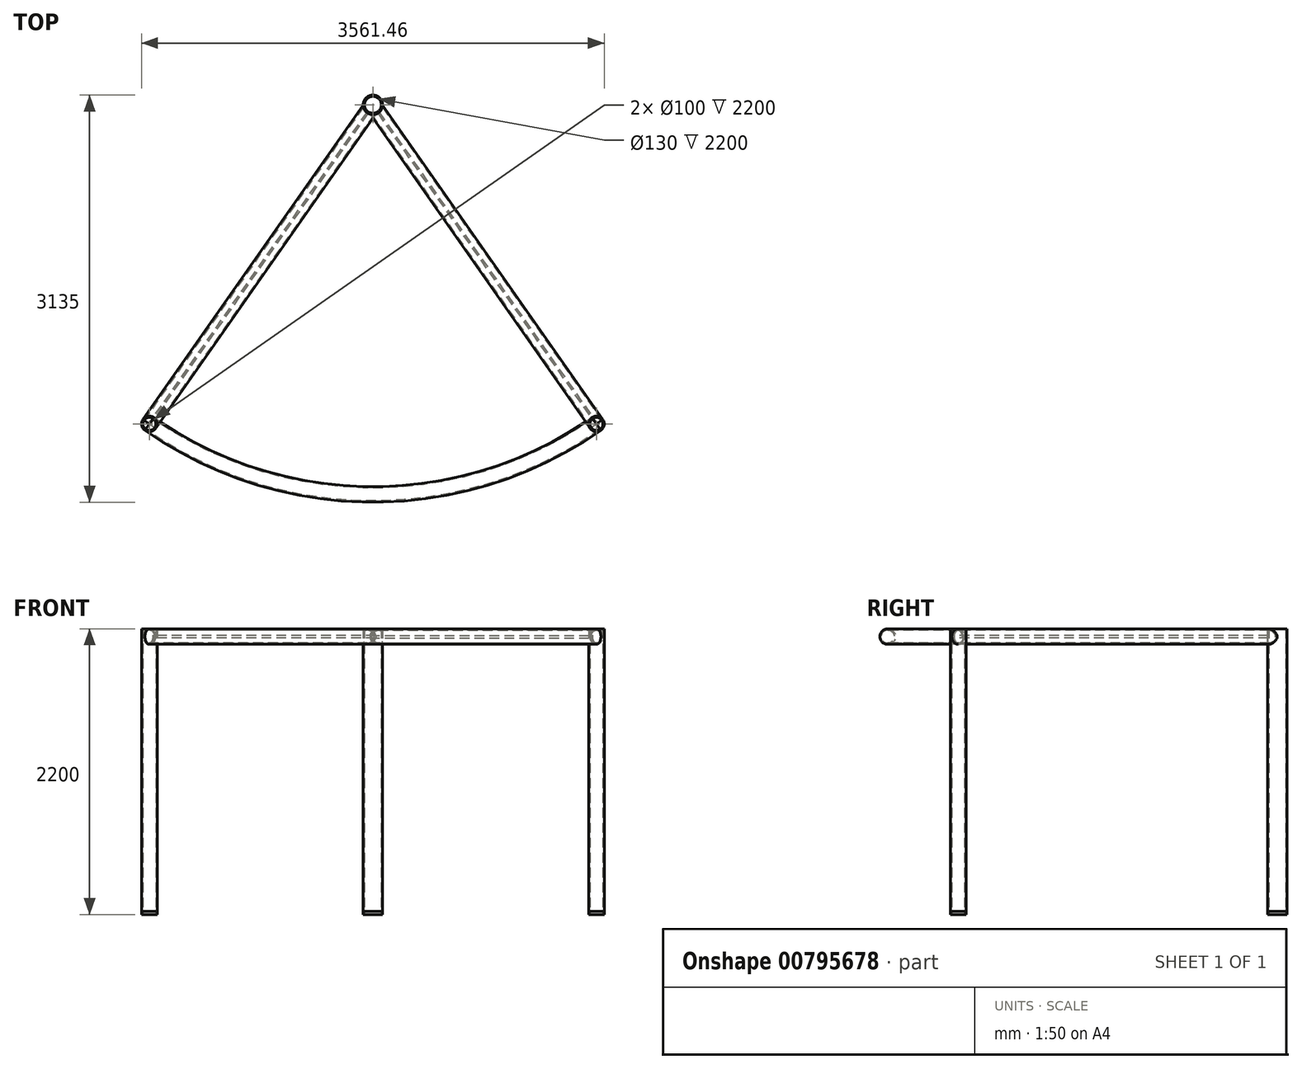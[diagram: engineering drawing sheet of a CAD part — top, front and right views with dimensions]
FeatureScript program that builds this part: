
annotation { "Feature Type Name" : "Feature", "Feature Type Description" : "" }
export const myFeature = defineFeature(function(context is Context, id is Id, definition is map)
    precondition{}
    {
        {
            var Q0;
            Q0=qCreatedBy(makeId("Front.planeOp"),FACE);
            var sketch = newSketch(context, id + "F0", { "sketchPlane" : qUnion([Q0])});
            skLineSegment(sketch, "E0.bottom", {"start": v(110, -110) * mm, "end": v(-110, -110) * mm});
            skLineSegment(sketch, "E0.top", {"start": v(110, 110) * mm, "end": v(-110, 110) * mm});
            skLineSegment(sketch, "E0.left", {"start": v(110, -110) * mm, "end": v(110, 110) * mm});
            skLineSegment(sketch, "E0.right", {"start": v(-110, -110) * mm, "end": v(-110, 110) * mm});
            skPoint(sketch, "E0.middle", {"position": v(0, 0) * mm});
            skSolve(sketch);
        }
        {
            var Q0;
            Q0 = qSketchRegion(id + "F0", true);
            extrude(context, id + "F1", {"entities" : qUnion([Q0]), "depth" : 3 * mm, "offsetDistance" : 25 * mm});
        }
        {
            var Q0;
            Q0=makeQuery(id+"F1.opExtrude","SWEPT_BODY",BODY,{"disambiguationData":[OSD([sQuery(id+"F0.wireOp",EDGE,"E0.bottom"),sQuery(id+"F0.wireOp",EDGE,"E0.top"),sQuery(id+"F0.wireOp",EDGE,"E0.left"),sQuery(id+"F0.wireOp",EDGE,"E0.right")])]});
            deleteBodies(context, id + "F2", {"entities" : qUnion([Q0])});
        }
        {
            var Q0;
            Q0=qCreatedBy(makeId("Top.planeOp"),FACE);
            var sketch = newSketch(context, id + "F3", { "sketchPlane" : qUnion([Q0])});
            skCircle(sketch, "E1", {"center": v(0, 0) * mm, "radius": 75 * mm});
            skCircle(sketch, "E2", {"center": v(0, 0) * mm, "radius": 65 * mm});
            skLineSegment(sketch, "E3", {"start": v(0, 400.3) * mm, "end": v(0, -3050.65) * mm, "construction": true});
            skLineSegment(sketch, "E4", {"start": v(-745.68, 0) * mm, "end": v(766.8, 0) * mm, "construction": true});
            skLineSegment(sketch, "E5", {"start": v(0, 0) * mm, "end": v(-1977.66, -2824.4) * mm, "construction": true});
            skLineSegment(sketch, "E6.MirrorCS", {"start": v(0, 0) * mm, "end": v(1977.66, -2824.4) * mm, "construction": true});
            skArc(sketch, "E7", {"start": v(-1720.73, -2457.46) * mm, "mid": v(0, -3000) * mm, "end": v(1720.73, -2457.46) * mm});
            skCircle(sketch, "E8", {"center": v(-1720.73, -2457.46) * mm, "radius": 60 * mm});
            skCircle(sketch, "E9", {"center": v(-1720.73, -2457.46) * mm, "radius": 50 * mm});
            skCircle(sketch, "E10.MirrorC", {"center": v(1720.73, -2457.46) * mm, "radius": 60 * mm});
            skCircle(sketch, "E11.MirrorC", {"center": v(1720.73, -2457.46) * mm, "radius": 50 * mm});
            skSolve(sketch);
        }
        {
            var Q0;
            Q0 = qSketchRegion(id + "F3", true);
            extrude(context, id + "F4", {"entities" : qUnion([Q0]), "depth" : 2200 * mm, "offsetDistance" : 25 * mm});
        }
        {
            var Q0;
            Q0 = qSketchRegion(id + "F3", true);
            extrude(context, id + "F5", {"entities" : qUnion([Q0]), "depth" : 25 * mm, "offsetDistance" : 25 * mm});
        }
        {
            var Q0;
            Q0=makeQuery(id+"F4.opExtrude","CAP_FACE",FACE,{"disambiguationData":[OSD([sQuery(id+"F3.wireOp",EDGE,"E1"),sQuery(id+"F3.wireOp",EDGE,"E2")])],"isStart":false});
            cPlane(context, id + "F6", {"entities" : qUnion([Q0]), "cplaneType" : CPlaneType.OFFSET, "offset" : 0 * mm, "width" : 150 * mm, "height" : 150 * mm});
        }
        {
            var Q0;
            Q0=sQuery(id+"F3.wireOp",EDGE,"E5");
            var Q1;
            Q1=sQuery(id+"F3.wireOp",VERTEX,"E7.start");
            cPlane(context, id + "F7", {"entities" : qUnion([Q0, Q1]), "cplaneType" : CPlaneType.LINE_POINT, "offset" : 25 * mm, "width" : 150 * mm, "height" : 150 * mm});
        }
        {
            var Q0;
            Q0=qCreatedBy(id+"F7.planeOp",FACE);
            var sketch = newSketch(context, id + "F8", { "sketchPlane" : qUnion([Q0])});
            skLineSegment(sketch, "E12.0", {"start": v(-60, 2200) * mm, "end": v(60, 2200) * mm});
            skLineSegment(sketch, "E13.bottom", {"start": v(-60, 2200) * mm, "end": v(59.3, 2200) * mm});
            skLineSegment(sketch, "E13.top", {"start": v(-60, 2080) * mm, "end": v(59.3, 2080) * mm});
            skLineSegment(sketch, "E13.left", {"start": v(-60, 2200) * mm, "end": v(-60, 2080) * mm});
            skLineSegment(sketch, "E13.right", {"start": v(59.3, 2200) * mm, "end": v(59.3, 2080) * mm});
            skPoint(sketch, "E14", {"position": v(-0.35, 2200) * mm});
            skLineSegment(sketch, "E15", {"start": v(0, 2210.44) * mm, "end": v(0, 2026.42) * mm, "construction": true});
            skLineSegment(sketch, "E16", {"start": v(-60, 2200) * mm, "end": v(59.3, 2080) * mm, "construction": true});
            skPoint(sketch, "E17", {"position": v(0, 2139.64) * mm});
            skCircle(sketch, "E18", {"center": v(0, 2139.64) * mm, "radius": 60 * mm});
            skCircle(sketch, "E19", {"center": v(0, 2139.64) * mm, "radius": 50 * mm});
            skSolve(sketch);
        }
        {
            var Q0;
            Q0=makeQuery(id+"F8.imprint","IMPRINT",FACE,{"disambiguationData":[TD([[makeQuery(id+"F8.imprint","IMPRINT",EDGE,{"derivedFrom":sQuery(id+"F8.wireOp",EDGE,"E19")}),-1.0]])]});
            var Q1;
            Q1=makeQuery(id+"F4.opExtrude","SWEPT_FACE",FACE,{"disambiguationData":[OSD([sQuery(id+"F3.wireOp",EDGE,"E1")])]});
            extrude(context, id + "F9", {"entities" : qUnion([Q0]), "endBound" : BoundingType.UP_TO_SURFACE, "oppositeDirection" : true, "depth" : 25 * mm, "endBoundEntityFace" : qUnion([Q1]), "offsetDistance" : 25 * mm});
        }
        {
            var Q0;
            Q0=makeQuery(id+"F9.opExtrude","SWEPT_BODY",BODY,{"disambiguationData":[OSD([sQuery(id+"F8.wireOp",EDGE,"E13.top"),sQuery(id+"F8.wireOp",EDGE,"E13.right"),sQuery(id+"F8.wireOp",EDGE,"E18"),sQuery(id+"F8.wireOp",EDGE,"E19")])]});
            var Q1;
            Q1=qCreatedBy(makeId("Right.planeOp"),FACE);
            mirror(context, id + "F10", {"entities" : qUnion([Q0]), "mirrorPlane" : qUnion([Q1])});
        }
        {
            var Q0;
            Q0=qCreatedBy(id+"F6.planeOp",FACE);
            var sketch = newSketch(context, id + "F11", { "sketchPlane" : qUnion([Q0])});
            skArc(sketch, "E20.0", {"start": v(-1720.73, -2457.46) * mm, "mid": v(0, -3000) * mm, "end": v(1720.73, -2457.46) * mm});
            skSolve(sketch);
        }
        {
            var Q0;
            Q0=qCreatedBy(makeId("Right.planeOp"),FACE);
            var sketch = newSketch(context, id + "F12", { "sketchPlane" : qUnion([Q0])});
            skPoint(sketch, "E21.0", {"position": v(-3000, 2200) * mm});
            skPoint(sketch, "E22.0", {"position": v(-3000, 0) * mm});
            skLineSegment(sketch, "E23", {"start": v(-3000, 0) * mm, "end": v(-3000, 2200) * mm, "construction": true});
            skPoint(sketch, "E24", {"position": v(-3000, 2140) * mm});
            skPoint(sketch, "E25", {"position": v(-3000, 60) * mm});
            skCircle(sketch, "E26", {"center": v(-3000, 2140) * mm, "radius": 60 * mm});
            skCircle(sketch, "E27", {"center": v(-3000, 60) * mm, "radius": 60 * mm});
            skCircle(sketch, "E28", {"center": v(-3000, 2140) * mm, "radius": 50 * mm});
            skCircle(sketch, "E29", {"center": v(-3000, 60) * mm, "radius": 50 * mm});
            skSolve(sketch);
        }
        {
            var Q0;
            Q0=makeQuery(id+"F12.imprint","IMPRINT",FACE,{"disambiguationData":[TD([[makeQuery(id+"F12.imprint","IMPRINT",EDGE,{"derivedFrom":sQuery(id+"F12.wireOp",EDGE,"E26")}),1.0]])]});
            var Q1;
            Q1=sQuery(id+"F11.wireOp",EDGE,"E20.0");
            sweep(context, id + "F13", {"profiles" : qUnion([Q0]), "path" : qUnion([Q1])});
        }
    });
